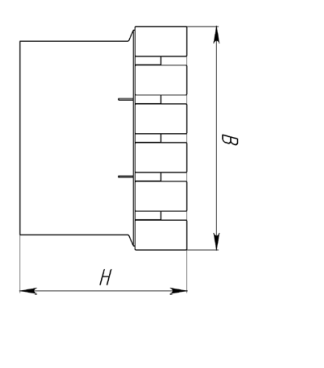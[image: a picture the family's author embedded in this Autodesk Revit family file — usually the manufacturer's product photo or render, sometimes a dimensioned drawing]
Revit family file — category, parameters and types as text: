
# Revit family: Скамейка стальная «Лондон» без спинки Арт 24379
name_source: partatom
category: Антураж
revit_build: Autodesk Revit 2018 (Build: 20180423_1000(x64)
units: mm (PartAtom-declared; Revit-internal decimal feet)

## family parameters
Всегда вертикально = Да
Источник визуального образа = Геометрия семейства
На основе рабочей плоскости = Нет
Общий = Нет
При загрузке вырезать с полостями = Нет
Точка расчета площади = Нет

## types (4) — shared parameters
Артикул товара = Арт. 24379
Высота = 450 мм
Группа модели = Скамейки
Изготовитель = ООО «Хоббика»
Материал изделия = Дерево, сталь
Цвет каркаса = Сталь
Цвет лавки = Орех
Ширина = 600 мм

## per-type parameters (varying)
| type | Версия 2,0 м | Версия 3,0 м | Версия 4,5 м | Версия 6,0 м | Длина |
| Скамейка стальная «Лондон» без спинки 2,0 м | Да | Нет | Нет | Нет | 2000 мм |
| Скамейка стальная «Лондон» без спинки 3,0 м | Нет | Да | Нет | Нет | 3000 мм |
| Скамейка стальная «Лондон» без спинки 4,5 м | Нет | Нет | Да | Нет | 4500 мм |
| Скамейка стальная «Лондон» без спинки 6,0 м | Нет | Нет | Нет | Да | 6000 мм |

note: column(s) folded — value = type name in every type: Описание
